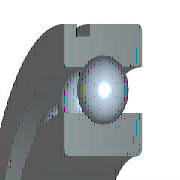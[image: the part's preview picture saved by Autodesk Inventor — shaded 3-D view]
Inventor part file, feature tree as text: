
AUTODESK INVENTOR PART (.ipt)
format: ipt  version: 2015 (Build 190159000, 159)  size: 310,784 bytes
history: native  units: mm (DEFAULTED — no unit token found)
features: sketch x1, other x1, pattern_circular x1
ambient origin geometry x8: Origin, YZ Plane, XZ Plane, XY Plane, X Axis, Y Axis, Z Axis, Center Point
bodies: Solid1 (feature_tree)
feature tree (3):
  sketch  "草图"  dims[d0=5.2mm d17=90.0deg d18=90.0deg d1=0.6mm d2=60.0mm d3=360.0deg d4=0.0mm d5=0.0mm d6=0.0mm d7=10.0mm d8=30.0mm d9=20.0mm d10=27.84mm d11=16.52mm d12=16.52mm d13=16.52mm d14=0.0mm d15=9.0mm d16=9.0mm d19=1.5mm d20=3.0mm d22=4.5mm d23=0.0mm d24=0.0mm]
  other  "轴承体"
  pattern_circular  "IDS_ARRAYBALL[SIMPL:T]"  Angle=90.0deg  [1 undecoded]
note: 1 required parameter value undecoded (feature->parameter linkage not recoverable at this tier; creation-order binding heuristic only, values carry confidence <= 0.55)
